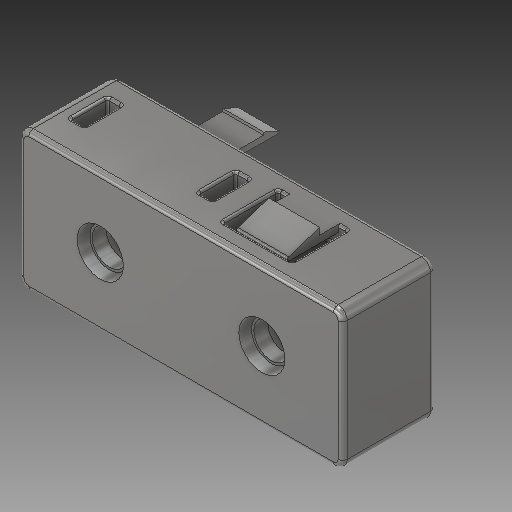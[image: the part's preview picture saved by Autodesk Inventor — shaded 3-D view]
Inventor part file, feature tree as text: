
AUTODESK INVENTOR PART (.ipt)
format: ipt  version: 2019 (Build 230136000, 136)  size: 515,584 bytes
history: native  units: in
note: dims shown in document units (in); Inventor stores cm internally (conversion verified against a paired STEP export)
features: sketch x23, other x3, plane x3
ambient origin geometry x8: Origin, YZ Plane, XZ Plane, XY Plane, X Axis, Y Axis, Z Axis, Center Point
bodies: Solid1 (feature_tree)
feature tree (29):
  other  "Power Switch Control.ipt"
  other  "Solid1::Power Switch Control.ipt"
  other  "TaggingFeature1"
  sketch  "Sketch1"  dims[d0=0.3937in]
  sketch  "Sketch2"
  sketch  "Sketch3"
  sketch  "Sketch4"
  sketch  "Sketch5"
  sketch  "Sketch6"
  sketch  "Sketch7"
  sketch  "Sketch8"
  sketch  "Sketch9"
  sketch  "Sketch10"
  sketch  "Sketch11"
  sketch  "Sketch12"
  sketch  "Sketch13"
  sketch  "Sketch14"
  sketch  "Sketch15"
  sketch  "Sketch16"
  sketch  "Sketch17"
  sketch  "Sketch18"
  sketch  "Sketch19"
  sketch  "Sketch20"
  sketch  "Sketch21"
  sketch  "Sketch22"
  sketch  "Sketch23"
  plane  "Work Plane1"
  plane  "Work Plane2"
  plane  "Work Plane3"
